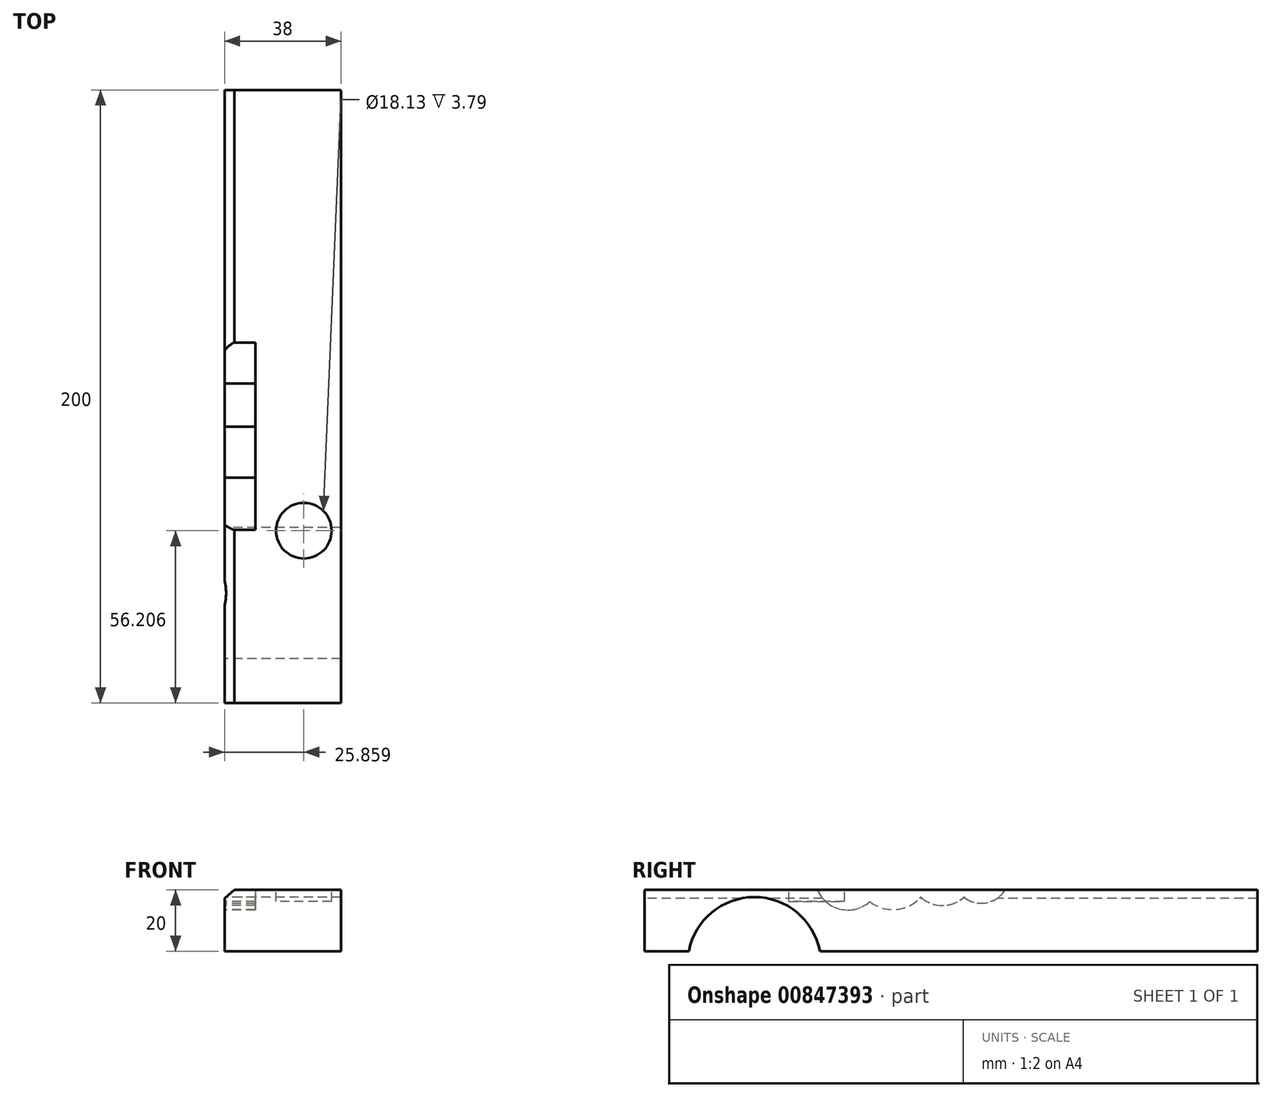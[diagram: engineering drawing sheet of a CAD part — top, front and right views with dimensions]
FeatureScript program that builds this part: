
annotation { "Feature Type Name" : "Feature", "Feature Type Description" : "" }
export const myFeature = defineFeature(function(context is Context, id is Id, definition is map)
    precondition{}
    {
        {
            var Q0;
            Q0=qCreatedBy(makeId("Right.planeOp"),FACE);
            var sketch = newSketch(context, id + "F0", { "sketchPlane" : qUnion([Q0])});
            skLineSegment(sketch, "E0", {"start": v(-62.3, -26.21) * mm, "end": v(-62.3, -46.21) * mm});
            skLineSegment(sketch, "E1", {"start": v(-62.3, -46.21) * mm, "end": v(137.7, -46.21) * mm});
            skLineSegment(sketch, "E2", {"start": v(137.7, -46.21) * mm, "end": v(137.7, -26.21) * mm});
            skLineSegment(sketch, "E3", {"start": v(137.7, -26.21) * mm, "end": v(-62.3, -26.21) * mm});
            skSolve(sketch);
        }
        {
            var Q0;
            Q0 = qSketchRegion(id + "F0", true);
            extrude(context, id + "F1", {"entities" : qUnion([Q0]), "depth" : 38 * mm, "offsetDistance" : 25 * mm});
        }
        {
            var Q0;
            Q0=qCreatedBy(makeId("Right.planeOp"),FACE);
            var sketch = newSketch(context, id + "F2", { "sketchPlane" : qUnion([Q0])});
            skCircle(sketch, "E4", {"center": v(-26.44, -50.35) * mm, "radius": 21.8 * mm});
            skSolve(sketch);
        }
        {
            var Q0;
            Q0 = qSketchRegion(id + "F2", true);
            extrude(context, id + "F3", {"entities" : qUnion([Q0]), "operationType" : NewBodyOperationType.REMOVE, "depth" : 90 * mm, "offsetDistance" : 25 * mm});
        }
        {
            var Q0;
            Q0=qCreatedBy(makeId("Right.planeOp"),FACE);
            var sketch = newSketch(context, id + "F4", { "sketchPlane" : qUnion([Q0])});
            skCircle(sketch, "E5", {"center": v(4.05, -22.05) * mm, "radius": 10.74 * mm});
            skCircle(sketch, "E6", {"center": v(18.74, -20.41) * mm, "radius": 12.24 * mm});
            skCircle(sketch, "E7", {"center": v(34.9, -20.78) * mm, "radius": 10.54 * mm});
            skCircle(sketch, "E8", {"center": v(47.6, -21.5) * mm, "radius": 9.07 * mm});
            skSolve(sketch);
        }
        {
            var Q0;
            Q0 = qSketchRegion(id + "F4", true);
            extrude(context, id + "F5", {"entities" : qUnion([Q0]), "operationType" : NewBodyOperationType.REMOVE, "depth" : 10 * mm, "offsetDistance" : 25 * mm});
        }
        {
            var Q0;
            Q0=qCreatedBy(makeId("Top.planeOp"),FACE);
            var sketch = newSketch(context, id + "F6", { "sketchPlane" : qUnion([Q0])});
            skCircle(sketch, "E9", {"center": v(25.86, -6.08) * mm, "radius": 9.06 * mm});
            skSolve(sketch);
        }
        {
            var Q0;
            Q0 = qSketchRegion(id + "F6", true);
            extrude(context, id + "F7", {"entities" : qUnion([Q0]), "operationType" : NewBodyOperationType.REMOVE, "oppositeDirection" : true, "depth" : 30 * mm, "offsetDistance" : 25 * mm});
        }
        {
            var Q0;
            Q0=qCreatedBy(makeId("Front.planeOp"),FACE);
            var sketch = newSketch(context, id + "F8", { "sketchPlane" : qUnion([Q0])});
            skLineSegment(sketch, "E10", {"start": v(3.8, -25.61) * mm, "end": v(-0.6, -29.51) * mm});
            skLineSegment(sketch, "E11", {"start": v(-0.6, -29.51) * mm, "end": v(-0.6, -25.7) * mm});
            skLineSegment(sketch, "E12", {"start": v(-0.6, -25.7) * mm, "end": v(3.8, -25.61) * mm});
            skSolve(sketch);
        }
        {
            var Q0;
            Q0 = qSketchRegion(id + "F8", true);
            extrude(context, id + "F9", {"entities" : qUnion([Q0]), "operationType" : NewBodyOperationType.REMOVE, "endBound" : BoundingType.SYMMETRIC, "oppositeDirection" : true, "depth" : 1000 * mm, "offsetDistance" : 25 * mm});
        }
    });
